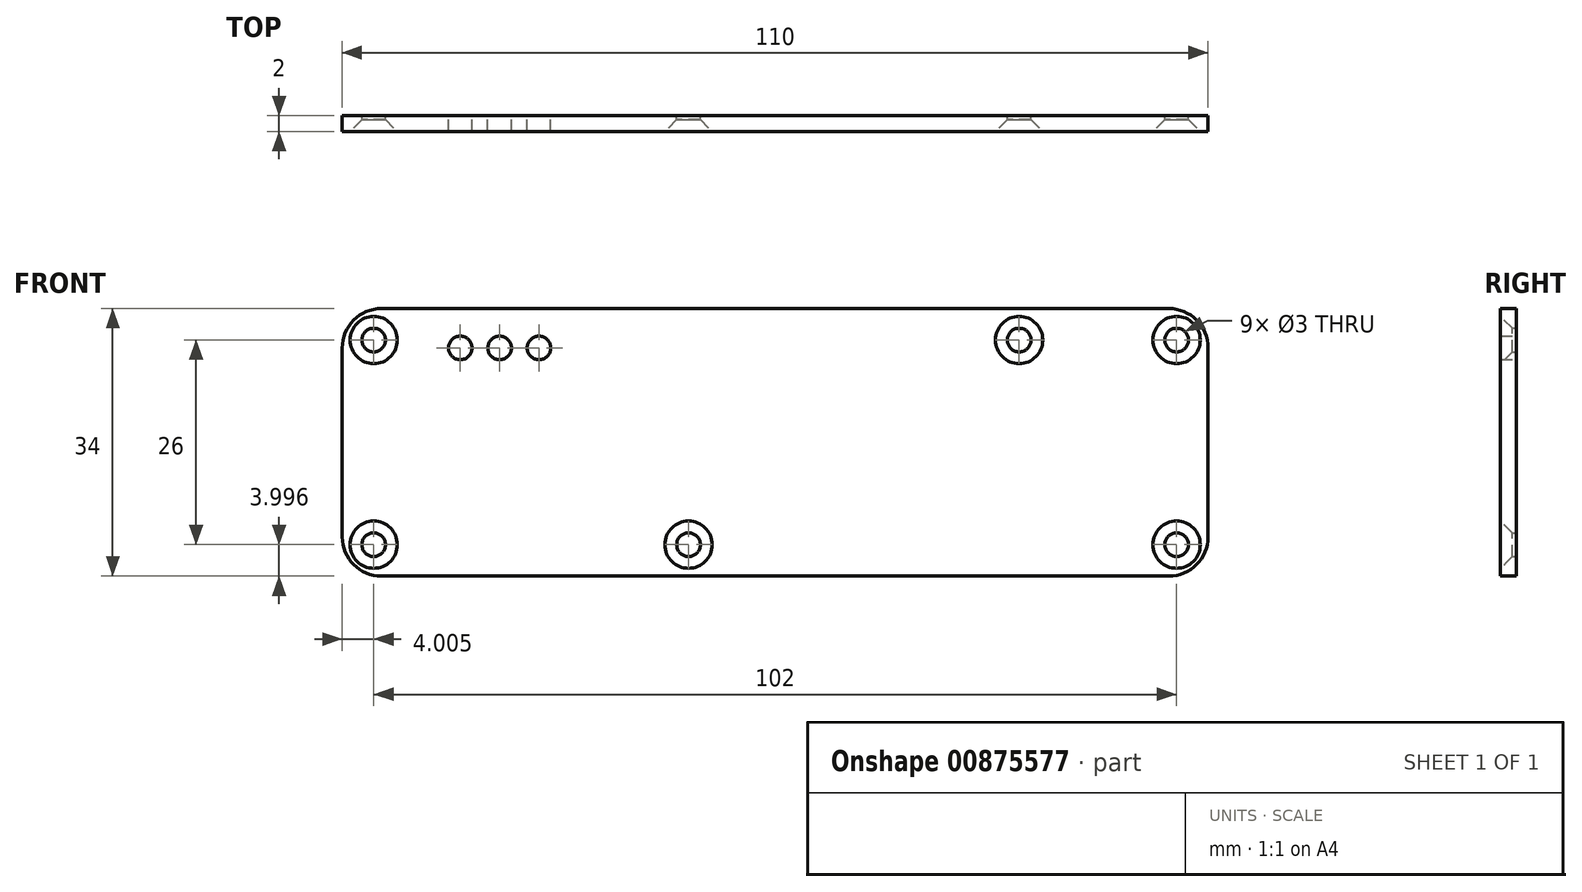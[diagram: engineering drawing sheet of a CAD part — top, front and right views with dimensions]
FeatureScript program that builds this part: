
annotation { "Feature Type Name" : "Feature", "Feature Type Description" : "" }
export const myFeature = defineFeature(function(context is Context, id is Id, definition is map)
    precondition{}
    {
        {
            var Q0;
            Q0=qCreatedBy(makeId("Front.planeOp"),FACE);
            var sketch = newSketch(context, id + "F0", { "sketchPlane" : qUnion([Q0])});
            skLineSegment(sketch, "E0.bottom", {"start": v(-44.22, 17.8) * mm, "end": v(55.78, 17.8) * mm});
            skLineSegment(sketch, "E0.top", {"start": v(-44.22, -16.2) * mm, "end": v(55.78, -16.2) * mm});
            skLineSegment(sketch, "E0.left", {"start": v(-49.22, 12.8) * mm, "end": v(-49.22, -11.2) * mm});
            skLineSegment(sketch, "E0.right", {"start": v(60.78, 12.8) * mm, "end": v(60.78, -11.2) * mm});
            skPoint(sketch, "E1.visualSharp", {"position": v(-49.22, 17.8) * mm});
            skArc(sketch, "E1.filletArc", {"start": v(-44.22, 17.8) * mm, "mid": v(-47.75, 16.33) * mm, "end": v(-49.22, 12.8) * mm});
            skPoint(sketch, "E2.visualSharp", {"position": v(-49.22, -16.2) * mm});
            skArc(sketch, "E2.filletArc", {"start": v(-49.22, -11.2) * mm, "mid": v(-47.75, -14.74) * mm, "end": v(-44.22, -16.2) * mm});
            skPoint(sketch, "E3.visualSharp", {"position": v(60.78, -16.2) * mm});
            skArc(sketch, "E3.filletArc", {"start": v(55.78, -16.2) * mm, "mid": v(59.32, -14.74) * mm, "end": v(60.78, -11.2) * mm});
            skPoint(sketch, "E4.visualSharp", {"position": v(60.78, 17.8) * mm});
            skArc(sketch, "E4.filletArc", {"start": v(60.78, 12.8) * mm, "mid": v(59.32, 16.33) * mm, "end": v(55.78, 17.8) * mm});
            skCircle(sketch, "E5", {"center": v(-34.22, 12.8) * mm, "radius": 1.5 * mm});
            skCircle(sketch, "E6", {"center": v(-29.22, 12.8) * mm, "radius": 1.5 * mm});
            skCircle(sketch, "E7", {"center": v(-24.22, 12.8) * mm, "radius": 1.5 * mm});
            skCircle(sketch, "E8", {"center": v(-45.22, 13.8) * mm, "radius": 1.5 * mm});
            skCircle(sketch, "E9", {"center": v(-45.22, -12.2) * mm, "radius": 1.5 * mm});
            skCircle(sketch, "E10", {"center": v(-5.22, -12.2) * mm, "radius": 1.5 * mm});
            skCircle(sketch, "E11", {"center": v(36.78, 13.8) * mm, "radius": 1.5 * mm});
            skCircle(sketch, "E12", {"center": v(56.78, 13.8) * mm, "radius": 1.5 * mm});
            skCircle(sketch, "E13", {"center": v(56.78, -12.2) * mm, "radius": 1.5 * mm});
            skSolve(sketch);
        }
        {
            var Q0;
            Q0 = qSketchRegion(id + "F0", true);
            extrude(context, id + "F1", {"entities" : qUnion([Q0]), "depth" : 2 * mm, "offsetDistance" : 25 * mm});
        }
        {
            var Q0;
            Q0=makeQuery(id+"F1.opExtrude","CAP_EDGE",EDGE,{"disambiguationData":[OSD([sQuery(id+"F0.wireOp",EDGE,"E8")])],"isStart":false});
            var Q1;
            Q1=makeQuery(id+"F1.opExtrude","CAP_EDGE",EDGE,{"disambiguationData":[OSD([sQuery(id+"F0.wireOp",EDGE,"E9")])],"isStart":false});
            var Q2;
            Q2=makeQuery(id+"F1.opExtrude","CAP_EDGE",EDGE,{"disambiguationData":[OSD([sQuery(id+"F0.wireOp",EDGE,"E10")])],"isStart":false});
            var Q3;
            Q3=makeQuery(id+"F1.opExtrude","CAP_EDGE",EDGE,{"disambiguationData":[OSD([sQuery(id+"F0.wireOp",EDGE,"E11")])],"isStart":false});
            var Q4;
            Q4=makeQuery(id+"F1.opExtrude","CAP_EDGE",EDGE,{"disambiguationData":[OSD([sQuery(id+"F0.wireOp",EDGE,"E12")])],"isStart":false});
            var Q5;
            Q5=makeQuery(id+"F1.opExtrude","CAP_EDGE",EDGE,{"disambiguationData":[OSD([sQuery(id+"F0.wireOp",EDGE,"E13")])],"isStart":false});
            chamfer(context, id + "F2", {"entities" : qUnion([Q0, Q1, Q2, Q3, Q4, Q5]), "width" : 1.5 * mm, "tangentPropagation" : true});
        }
    });
